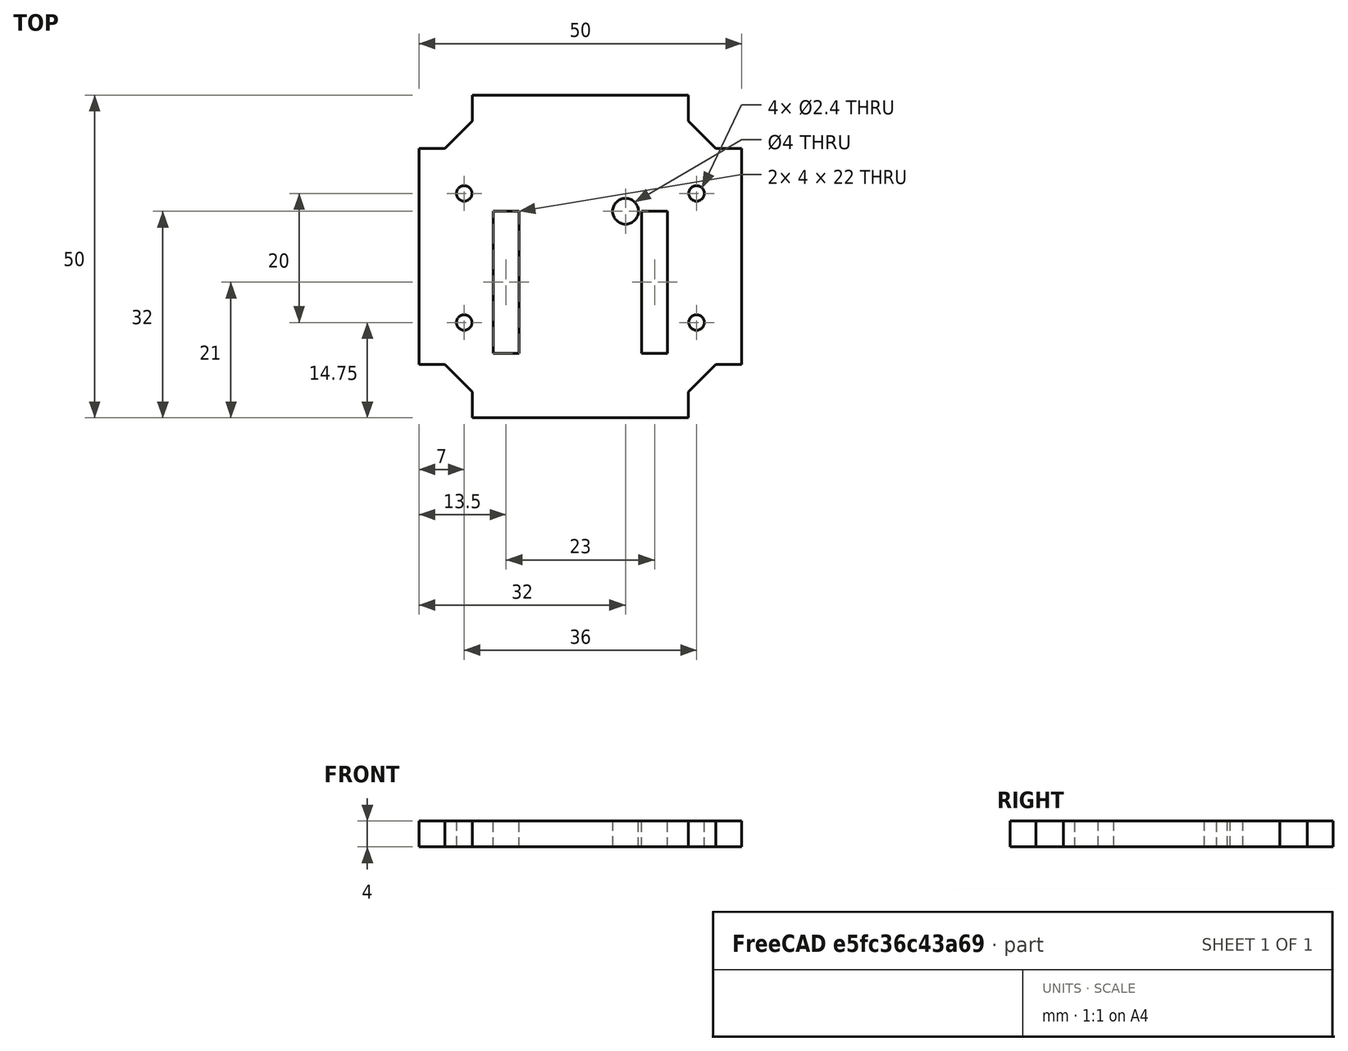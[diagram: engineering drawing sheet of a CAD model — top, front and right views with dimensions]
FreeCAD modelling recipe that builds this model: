
FCSTD DOCUMENT  (FreeCAD 0.19R24291 (Git))
Label: ESPCam Rear Plate
License: All rights reserved
LicenseURL: http://en.wikipedia.org/wiki/All_rights_reserved
objects: Sketcher::SketchObject×1, PartDesign::Pad×1, PartDesign::Body×1
note: 4 computed .brp shape members not serialized (recipe doc carries the construction recipe); baked Part::Feature solids carry a one-line shape summary decoded from their .brp

FEATURE [Sketcher::SketchObject] Sketch
  FullyConstrained = true
  MapMode = 5
  Support = -> [XY_Plane]
  sketch-geometry (41):
    g0: LineSegment StartX=0 StartY=0 StartZ=0 EndX=33.5 EndY=0 EndZ=0
    g1: LineSegment StartX=33.5 StartY=0 StartZ=0 EndX=33.5 EndY=4 EndZ=0
    g2: LineSegment StartX=33.5 StartY=4 StartZ=0 EndX=37.75 EndY=8.25 EndZ=0
    g3: LineSegment StartX=37.75 StartY=8.25 StartZ=0 EndX=41.75 EndY=8.25 EndZ=0
    g4: LineSegment StartX=41.75 StartY=8.25 StartZ=0 EndX=41.75 EndY=41.75 EndZ=0
    g5: LineSegment StartX=41.75 StartY=41.75 StartZ=0 EndX=37.75 EndY=41.75 EndZ=0
    g6: LineSegment StartX=37.75 StartY=41.75 StartZ=0 EndX=33.5 EndY=46 EndZ=0
    g7: LineSegment StartX=33.5 StartY=46 StartZ=0 EndX=33.5 EndY=50 EndZ=0
    g8: LineSegment StartX=33.5 StartY=50 StartZ=0 EndX=0 EndY=50 EndZ=0
    g9: LineSegment StartX=0 StartY=50 StartZ=0 EndX=0 EndY=46 EndZ=0
    g10: LineSegment StartX=0 StartY=46 StartZ=0 EndX=-4.25 EndY=41.75 EndZ=0
    g11: LineSegment StartX=-4.25 StartY=41.75 StartZ=0 EndX=-8.25 EndY=41.75 EndZ=0
    g12: LineSegment StartX=-8.25 StartY=41.75 StartZ=0 EndX=-8.25 EndY=8.25 EndZ=0
    g13: LineSegment StartX=-8.25 StartY=8.25 StartZ=0 EndX=-4.25 EndY=8.25 EndZ=0
    g14: LineSegment StartX=-4.25 StartY=8.25 StartZ=0 EndX=0 EndY=4 EndZ=0
    g15: LineSegment StartX=0 StartY=4 StartZ=0 EndX=0 EndY=0 EndZ=0
    g16: LineSegment StartX=0 StartY=46 StartZ=0 EndX=0 EndY=4 EndZ=0
    g17: LineSegment StartX=-4.25 StartY=8.25 StartZ=0 EndX=37.75 EndY=8.25 EndZ=0
    g18: LineSegment StartX=-4.25 StartY=41.75 StartZ=0 EndX=37.75 EndY=41.75 EndZ=0
    g19: LineSegment StartX=33.5 StartY=46 StartZ=0 EndX=33.5 EndY=4 EndZ=0
    g20: Circle CenterX=-1.25 CenterY=34.75 CenterZ=0 NormalX=0 NormalY=0 NormalZ=1 AngleXU=0 Radius=1.2
    g21: Circle CenterX=-1.25 CenterY=14.75 CenterZ=0 NormalX=0 NormalY=0 NormalZ=1 AngleXU=0 Radius=1.2
    g22: Circle CenterX=34.75 CenterY=14.75 CenterZ=0 NormalX=0 NormalY=0 NormalZ=1 AngleXU=0 Radius=1.2
    g23: Circle CenterX=34.75 CenterY=34.75 CenterZ=0 NormalX=0 NormalY=0 NormalZ=1 AngleXU=0 Radius=1.2
    g24: LineSegment StartX=-1.25 StartY=34.75 StartZ=0 EndX=34.75 EndY=34.75 EndZ=0
    g25: LineSegment StartX=34.75 StartY=34.75 StartZ=0 EndX=34.75 EndY=14.75 EndZ=0
    g26: LineSegment StartX=34.75 StartY=14.75 StartZ=0 EndX=-1.25 EndY=14.75 EndZ=0
    g27: LineSegment StartX=-1.25 StartY=14.75 StartZ=0 EndX=-1.25 EndY=34.75 EndZ=0
    g28: LineSegment StartX=-8.25 StartY=41.75 StartZ=0 EndX=41.75 EndY=8.25 EndZ=0
    g29: LineSegment StartX=41.75 StartY=41.75 StartZ=0 EndX=-8.25 EndY=8.25 EndZ=0
    g30: GeomPoint X=16.75 Y=25 Z=0
    g31: LineSegment StartX=3.25 StartY=32 StartZ=0 EndX=7.25 EndY=32 EndZ=0
    g32: LineSegment StartX=7.25 StartY=32 StartZ=0 EndX=7.25 EndY=10 EndZ=0
    g33: LineSegment StartX=7.25 StartY=10 StartZ=0 EndX=3.25 EndY=10 EndZ=0
    g34: LineSegment StartX=3.25 StartY=10 StartZ=0 EndX=3.25 EndY=32 EndZ=0
    g35: LineSegment StartX=30.25 StartY=32 StartZ=0 EndX=26.25 EndY=32 EndZ=0
    g36: LineSegment StartX=26.25 StartY=32 StartZ=0 EndX=26.25 EndY=10 EndZ=0
    g37: LineSegment StartX=26.25 StartY=10 StartZ=0 EndX=30.25 EndY=10 EndZ=0
    g38: LineSegment StartX=30.25 StartY=10 StartZ=0 EndX=30.25 EndY=32 EndZ=0
    g39: Circle CenterX=23.75 CenterY=32 CenterZ=0 NormalX=0 NormalY=0 NormalZ=1 AngleXU=0 Radius=2
    g40: LineSegment StartX=23.75 StartY=32 StartZ=0 EndX=26.25 EndY=32 EndZ=0
  constraints (110):
    c: Coincident(g0,g-1)
    c: PointOnObject(g0,g-1)
    c: Coincident(g1,g0)
    c: Coincident(g2,g1)
    c: Coincident(g3,g2)
    c: Vertical(g4)
    c: Coincident(g5,g4)
    c: Coincident(g6,g5)
    c: Coincident(g7,g6)
    c: Coincident(g8,g7)
    c: PointOnObject(g8,g-2)
    c: Horizontal(g8)
    c: Coincident(g9,g8)
    c: PointOnObject(g9,g-2)
    c: Coincident(g10,g9)
    c: Coincident(g11,g10)
    c: Coincident(g12,g11)
    c: Vertical(g12)
    c: Coincident(g13,g12)
    c: Coincident(g14,g13)
    c: PointOnObject(g14,g-2)
    c: Coincident(g15,g14)
    c: Coincident(g15,g0)
    c: Coincident(g16,g9)
    c: Coincident(g16,g14)
    c: Coincident(g17,g13)
    c: Coincident(g17,g2)
    c: Horizontal(g17)
    c: Coincident(g18,g10)
    c: Coincident(g18,g5)
    c: Horizontal(g18)
    c: Coincident(g19,g6)
    c: Coincident(g19,g1)
    c: Vertical(g19)
    c: Horizontal(g5)
    c: Horizontal(g3)
    c: Vertical(g1)
    c: Vertical(g7)
    c: Horizontal(g11)
    c: Horizontal(g13)
    c: DistanceX(g8,g8) = 33.5
    c: DistanceX(g11,g4) = 50
    c: Coincident(g3,g4)
    c: DistanceY(g0,g7) = 50
    c: Equal(g9,g11)
    c: Equal(g11,g13)
    c: Equal(g13,g15)
    c: Equal(g15,g1)
    c: Equal(g1,g3)
    c: Equal(g3,g5)
    c: Equal(g5,g7)
    c: Equal(g6,g10)
    c: Equal(g10,g14)
    c: DistanceY(g9,g9) = 4
    c: DistanceY(g4,g4) = 33.5
    c: Coincident(g24,g20)
    c: Coincident(g24,g23)
    c: Coincident(g25,g23)
    c: Coincident(g25,g22)
    c: Coincident(g26,g22)
    c: Coincident(g26,g21)
    c: Coincident(g27,g21)
    c: Coincident(g27,g20)
    c: Vertical(g27)
    c: Vertical(g25)
    c: Horizontal(g24)
    c: Horizontal(g26)
    c: DistanceY(g27,g27) = 20
    c: DistanceY(g12,g21) = 6.5
    c: DistanceX(g11,g20) = 7
    c: DistanceX(g23,g4) = 7
    c: Diameter(g20) = 2.4
    c: Equal(g20,g21)
    c: Equal(g21,g22)
    c: Equal(g22,g23)
    c: Coincident(g28,g11)
    c: Coincident(g28,g3)
    c: Coincident(g29,g4)
    c: Coincident(g29,g12)
    c: PointOnObject(g30,g28)
    c: PointOnObject(g30,g29)
    c: Coincident(g31,g32)
    c: Coincident(g32,g33)
    c: Coincident(g33,g34)
    c: Coincident(g34,g31)
    c: Horizontal(g31)
    c: Horizontal(g33)
    c: Vertical(g32)
    c: Vertical(g34)
    c: Coincident(g35,g36)
    c: Coincident(g36,g37)
    c: Coincident(g37,g38)
    c: Coincident(g38,g35)
    c: Horizontal(g35)
    c: Horizontal(g37)
    c: Vertical(g36)
    c: Vertical(g38)
    c: DistanceY(g30,g31) = 7
    c: DistanceY(g32,g32) = 22
    c: DistanceY(g30,g35) = 7
    c: DistanceY(g36,g36) = 22
    c: DistanceX(g31,g30) = 13.5
    c: DistanceX(g30,g35) = 13.5
    c: DistanceX(g31,g31) = 4
    c: DistanceX(g35,g35) = 4
    c: Diameter(g39) = 4
    c: DistanceX(g39,g35) = 2.5
    c: Coincident(g40,g39)
    c: Coincident(g40,g35)
    c: Horizontal(g40)
FEATURE [PartDesign::Pad] Pad
  Direction = (1,1,1)
  Length = 4
  Length2 = 100
  Profile = -> Sketch
  Type = 0
FEATURE [PartDesign::Body] Body
  Group = -> [Sketch,Pad]
  Origin = -> Origin
  Tip = -> Pad
